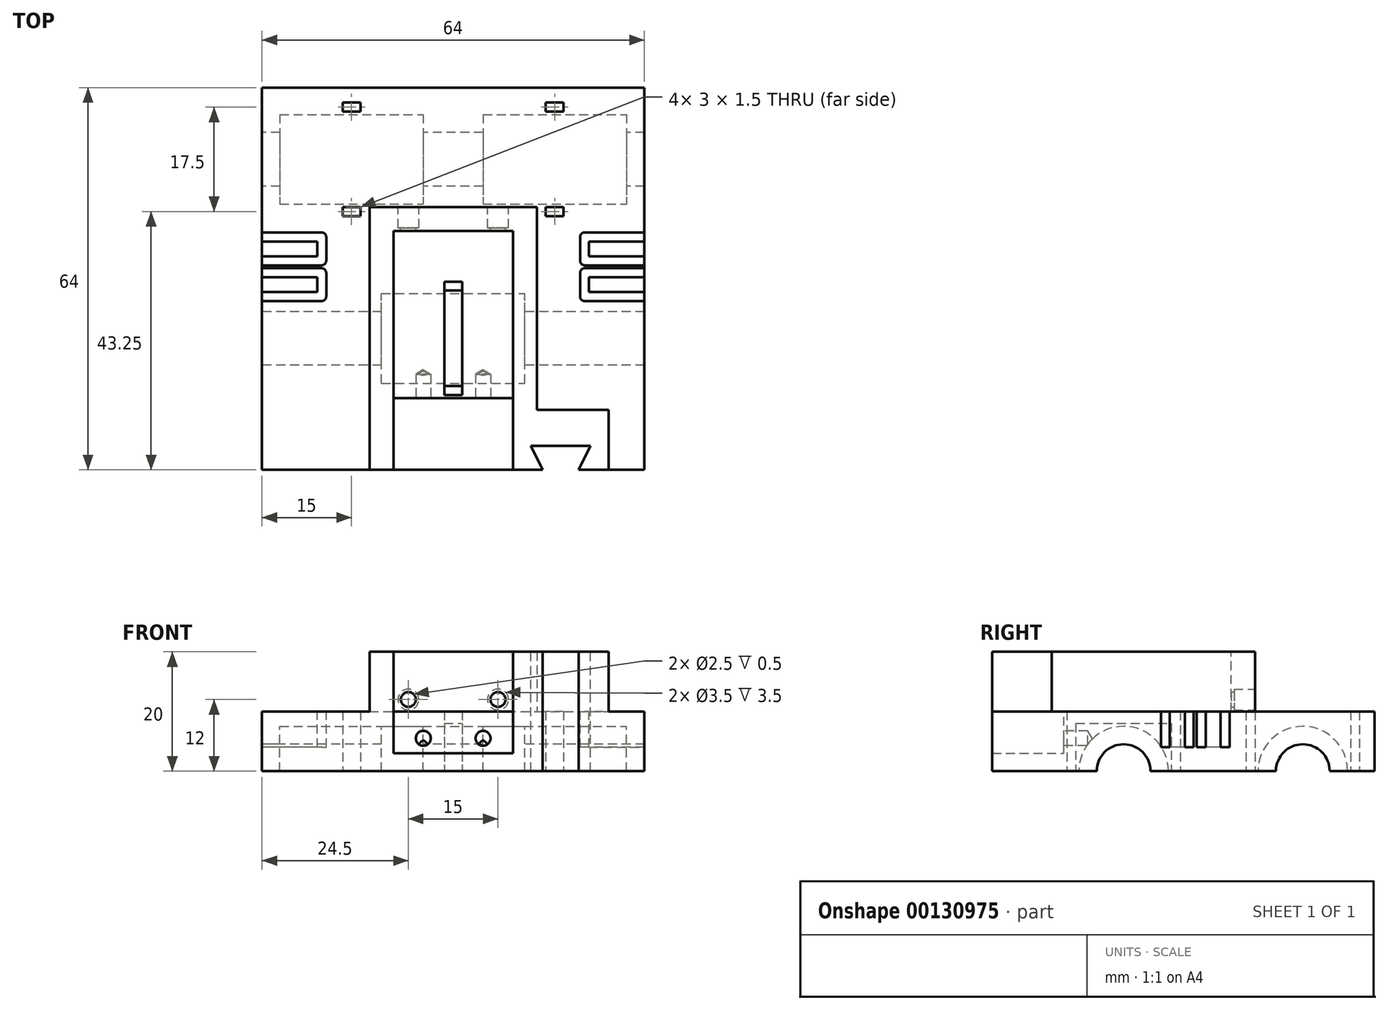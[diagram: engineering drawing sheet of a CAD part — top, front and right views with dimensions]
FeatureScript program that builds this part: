
annotation { "Feature Type Name" : "Feature", "Feature Type Description" : "" }
export const myFeature = defineFeature(function(context is Context, id is Id, definition is map)
    precondition{}
    {
        {
            var Q0;
            Q0=qCreatedBy(makeId("Top.planeOp"),FACE);
            var sketch = newSketch(context, id + "F0", { "sketchPlane" : qUnion([Q0])});
            skLineSegment(sketch, "E0.bottom", {"start": v(0, 0) * mm, "end": v(64, 0) * mm});
            skLineSegment(sketch, "E0.top", {"start": v(0, 64) * mm, "end": v(64, 64) * mm});
            skLineSegment(sketch, "E0.left", {"start": v(0, 0) * mm, "end": v(0, 64) * mm});
            skLineSegment(sketch, "E0.right", {"start": v(64, 0) * mm, "end": v(64, 64) * mm});
            skSolve(sketch);
        }
        {
            var Q0;
            Q0 = qSketchRegion(id + "F0", true);
            extrude(context, id + "F1", {"entities" : qUnion([Q0]), "depth" : 10 * mm});
        }
        {
            var Q0;
            Q0=makeQuery(id+"F1.opExtrude","SWEPT_FACE",FACE,{"disambiguationData":[OSD([sQuery(id+"F0.wireOp",EDGE,"E0.right")])]});
            var sketch = newSketch(context, id + "F2", { "sketchPlane" : qUnion([Q0])});
            skLineSegment(sketch, "E1", {"start": v(37, 15) * mm, "end": v(37, 0) * mm});
            skCircle(sketch, "E2", {"center": v(22, 0) * mm, "radius": 7.5 * mm});
            skCircle(sketch, "E3", {"center": v(52, 0) * mm, "radius": 7.5 * mm});
            skSolve(sketch);
        }
        {
            var Q0;
            {var subQ0=sQuery(id+"F2.wireOp",EDGE,"E2");var subQ1=makeQuery(id+"F1.opExtrude","CAP_EDGE",EDGE,{"disambiguationData":[OSD([sQuery(id+"F0.wireOp",EDGE,"E0.right")])],"isStart":true});var subQ2=makeQuery(id+"F2.imprint","INTERSECT",VERTEX,{"disambiguationData":[OD(0.0)],"derivedFrom":[subQ1,subQ0]});Q0=makeQuery(id+"F2.imprint","IMPRINT",FACE,{"disambiguationData":[TD([[makeQuery(id+"F2.imprint","IMPRINT",EDGE,{"disambiguationData":[TD([[subQ2,1.0]])],"derivedFrom":subQ0}),1.0]])]});}
            var Q1;
            {var subQ0=sQuery(id+"F2.wireOp",EDGE,"E3");var subQ1=makeQuery(id+"F1.opExtrude","CAP_EDGE",EDGE,{"disambiguationData":[OSD([sQuery(id+"F0.wireOp",EDGE,"E0.right")])],"isStart":true});var subQ2=makeQuery(id+"F2.imprint","INTERSECT",VERTEX,{"disambiguationData":[OD(0.0)],"derivedFrom":[subQ1,subQ0]});Q1=makeQuery(id+"F2.imprint","IMPRINT",FACE,{"disambiguationData":[TD([[makeQuery(id+"F2.imprint","IMPRINT",EDGE,{"disambiguationData":[TD([[subQ2,-1.0]])],"derivedFrom":subQ0}),1.0]])]});}
            extrude(context, id + "F3", {"entities" : qUnion([Q0, Q1]), "operationType" : NewBodyOperationType.REMOVE, "endBound" : BoundingType.THROUGH_ALL, "oppositeDirection" : true, "depth" : 25 * mm});
        }
        {
            var Q0;
            {var subQ0=sQuery(id+"F0.wireOp",EDGE,"E0.bottom");var subQ1=sQuery(id+"F0.wireOp",EDGE,"E0.left");var subQ2=sQuery(id+"F0.wireOp",EDGE,"E0.right");Q0=makeQuery(id+"F3.boolean.opBoolean","SPLIT",FACE,{"disambiguationData":[TD([makeQuery(id+"F1.opExtrude","SWEPT_FACE",FACE,{"disambiguationData":[OSD([subQ0])]}),makeQuery(id+"F1.opExtrude","SWEPT_FACE",FACE,{"disambiguationData":[OSD([subQ1])]}),makeQuery(id+"F1.opExtrude","SWEPT_FACE",FACE,{"disambiguationData":[OSD([subQ2])]}),makeQuery(id+"F3.opExtrude","SWEPT_FACE",FACE,{"disambiguationData":[OSD([sQuery(id+"F2.wireOp",EDGE,"E2")])]})])],"derivedFrom":makeQuery(id+"F1.opExtrude","CAP_FACE",FACE,{"disambiguationData":[OSD([subQ0,sQuery(id+"F0.wireOp",EDGE,"E0.top"),subQ1,subQ2])],"isStart":true})});}
            var sketch = newSketch(context, id + "F4", { "sketchPlane" : qUnion([Q0])});
            skLineSegment(sketch, "E4.bottom", {"start": v(0, 0) * mm, "end": v(20, 0) * mm});
            skLineSegment(sketch, "E4.top", {"start": v(0, -34.5) * mm, "end": v(20, -34.5) * mm});
            skLineSegment(sketch, "E4.left", {"start": v(0, 0) * mm, "end": v(0, -34.5) * mm});
            skLineSegment(sketch, "E4.right", {"start": v(20, 0) * mm, "end": v(20, -34.5) * mm});
            skLineSegment(sketch, "E5.bottom", {"start": v(64, 0) * mm, "end": v(44, 0) * mm});
            skLineSegment(sketch, "E5.top", {"start": v(64, -34.5) * mm, "end": v(44, -34.5) * mm});
            skLineSegment(sketch, "E5.left", {"start": v(64, 0) * mm, "end": v(64, -34.5) * mm});
            skLineSegment(sketch, "E5.right", {"start": v(44, 0) * mm, "end": v(44, -34.5) * mm});
            skSolve(sketch);
        }
        {
            var Q0;
            {var subQ0=sQuery(id+"F0.wireOp",EDGE,"E0.top");var subQ1=sQuery(id+"F0.wireOp",EDGE,"E0.left");var subQ2=sQuery(id+"F0.wireOp",EDGE,"E0.right");Q0=makeQuery(id+"F3.boolean.opBoolean","SPLIT",FACE,{"disambiguationData":[TD([makeQuery(id+"F1.opExtrude","SWEPT_FACE",FACE,{"disambiguationData":[OSD([subQ0])]}),makeQuery(id+"F1.opExtrude","SWEPT_FACE",FACE,{"disambiguationData":[OSD([subQ1])]}),makeQuery(id+"F1.opExtrude","SWEPT_FACE",FACE,{"disambiguationData":[OSD([subQ2])]}),makeQuery(id+"F3.opExtrude","SWEPT_FACE",FACE,{"disambiguationData":[OSD([sQuery(id+"F2.wireOp",EDGE,"E3")])]})])],"derivedFrom":makeQuery(id+"F1.opExtrude","CAP_FACE",FACE,{"disambiguationData":[OSD([sQuery(id+"F0.wireOp",EDGE,"E0.bottom"),subQ0,subQ1,subQ2])],"isStart":true})});}
            var sketch = newSketch(context, id + "F5", { "sketchPlane" : qUnion([Q0])});
            skLineSegment(sketch, "E6.bottom", {"start": v(0, -64) * mm, "end": v(3, -64) * mm});
            skLineSegment(sketch, "E6.top", {"start": v(0, -37.3) * mm, "end": v(3, -37.3) * mm});
            skLineSegment(sketch, "E6.left", {"start": v(0, -64) * mm, "end": v(0, -37.3) * mm});
            skLineSegment(sketch, "E6.right", {"start": v(3, -64) * mm, "end": v(3, -37.3) * mm});
            skLineSegment(sketch, "E7.bottom", {"start": v(27, -64) * mm, "end": v(37, -64) * mm});
            skLineSegment(sketch, "E7.top", {"start": v(27, -37.3) * mm, "end": v(37, -37.3) * mm});
            skLineSegment(sketch, "E7.left", {"start": v(27, -64) * mm, "end": v(27, -37.3) * mm});
            skLineSegment(sketch, "E7.right", {"start": v(37, -64) * mm, "end": v(37, -37.3) * mm});
            skLineSegment(sketch, "E8.bottom", {"start": v(64, -64) * mm, "end": v(61, -64) * mm});
            skLineSegment(sketch, "E8.top", {"start": v(64, -37.3) * mm, "end": v(61, -37.3) * mm});
            skLineSegment(sketch, "E8.left", {"start": v(64, -64) * mm, "end": v(64, -37.3) * mm});
            skLineSegment(sketch, "E8.right", {"start": v(61, -64) * mm, "end": v(61, -37.3) * mm});
            skSolve(sketch);
        }
        {
            var Q0;
            Q0 = qSketchRegion(id + "F4", true);
            var Q1;
            Q1 = qSketchRegion(id + "F5", true);
            extrude(context, id + "F6", {"entities" : qUnion([Q0, Q1]), "operationType" : NewBodyOperationType.ADD, "oppositeDirection" : true, "depth" : 7.6 * mm});
        }
        {
            var Q0;
            Q0=makeQuery(id+"F6.boolean.opBoolean","MERGE",FACE,{"derivedFrom":[makeQuery(id+"F1.opExtrude","SWEPT_FACE",FACE,{"disambiguationData":[OSD([sQuery(id+"F0.wireOp",EDGE,"E0.left")])]}),makeQuery(id+"F6.opExtrude","SWEPT_FACE",FACE,{"disambiguationData":[OSD([sQuery(id+"F4.wireOp",EDGE,"E4.left")])]}),makeQuery(id+"F6.opExtrude","SWEPT_FACE",FACE,{"disambiguationData":[OSD([sQuery(id+"F5.wireOp",EDGE,"E6.left")])]})]});
            var sketch = newSketch(context, id + "F7", { "sketchPlane" : qUnion([Q0])});
            skLineSegment(sketch, "E9", {"start": v(-37, 15) * mm, "end": v(-37, 0) * mm});
            skCircle(sketch, "E10", {"center": v(-52, 0) * mm, "radius": 4.5 * mm});
            skCircle(sketch, "E11", {"center": v(-22, 0) * mm, "radius": 4.5 * mm});
            skSolve(sketch);
        }
        {
            var Q0;
            Q0 = qSketchRegion(id + "F7", true);
            extrude(context, id + "F8", {"entities" : qUnion([Q0]), "operationType" : NewBodyOperationType.REMOVE, "endBound" : BoundingType.THROUGH_ALL, "oppositeDirection" : true, "depth" : 25 * mm});
        }
        {
            var Q0;
            Q0=makeQuery(id+"F1.opExtrude","CAP_FACE",FACE,{"disambiguationData":[OSD([sQuery(id+"F0.wireOp",EDGE,"E0.bottom"),sQuery(id+"F0.wireOp",EDGE,"E0.top"),sQuery(id+"F0.wireOp",EDGE,"E0.left"),sQuery(id+"F0.wireOp",EDGE,"E0.right")])],"isStart":false});
            var sketch = newSketch(context, id + "F9", { "sketchPlane" : qUnion([Q0])});
            skLineSegment(sketch, "E12.bottom", {"start": v(18, 0) * mm, "end": v(58, 0) * mm});
            skLineSegment(sketch, "E12.top", {"start": v(18, 44) * mm, "end": v(58, 44) * mm});
            skLineSegment(sketch, "E12.left", {"start": v(18, 0) * mm, "end": v(18, 44) * mm});
            skLineSegment(sketch, "E12.right", {"start": v(58, 0) * mm, "end": v(58, 44) * mm});
            skLineSegment(sketch, "E13.bottom", {"start": v(46, 44) * mm, "end": v(58, 44) * mm});
            skLineSegment(sketch, "E13.top", {"start": v(46, 10) * mm, "end": v(58, 10) * mm});
            skLineSegment(sketch, "E13.left", {"start": v(46, 44) * mm, "end": v(46, 10) * mm});
            skLineSegment(sketch, "E13.right", {"start": v(58, 44) * mm, "end": v(58, 10) * mm});
            skSolve(sketch);
        }
        {
            var Q0;
            Q0=makeQuery(id+"F9.imprint","IMPRINT",FACE,{"disambiguationData":[TD([[makeQuery(id+"F9.imprint","IMPRINT",EDGE,{"derivedFrom":sQuery(id+"F9.wireOp",EDGE,"E12.bottom")}),1.0]])]});
            extrude(context, id + "F10", {"entities" : qUnion([Q0]), "operationType" : NewBodyOperationType.ADD, "depth" : 10 * mm});
        }
        {
            var Q0;
            Q0=makeQuery(id+"F10.opExtrude","CAP_FACE",FACE,{"disambiguationData":[OSD([sQuery(id+"F9.wireOp",EDGE,"E12.bottom"),sQuery(id+"F9.wireOp",EDGE,"E12.top"),sQuery(id+"F9.wireOp",EDGE,"E12.left"),sQuery(id+"F9.wireOp",EDGE,"E12.right")])],"isStart":false});
            var sketch = newSketch(context, id + "F11", { "sketchPlane" : qUnion([Q0])});
            skLineSegment(sketch, "E14.bottom", {"start": v(22, 0) * mm, "end": v(42, 0) * mm});
            skLineSegment(sketch, "E14.top", {"start": v(22, 40) * mm, "end": v(42, 40) * mm});
            skLineSegment(sketch, "E14.left", {"start": v(22, 0) * mm, "end": v(22, 40) * mm});
            skLineSegment(sketch, "E14.right", {"start": v(42, 0) * mm, "end": v(42, 40) * mm});
            skSolve(sketch);
        }
        {
            var Q0;
            Q0 = qSketchRegion(id + "F11", true);
            extrude(context, id + "F12", {"entities" : qUnion([Q0]), "operationType" : NewBodyOperationType.REMOVE, "oppositeDirection" : true, "depth" : 10 * mm});
        }
        {
            var Q0;
            Q0=makeQuery(id+"F12.boolean.opBoolean","COPY",FACE,{"derivedFrom":makeQuery(id+"F12.opExtrude","CAP_FACE",FACE,{"disambiguationData":[OSD([sQuery(id+"F11.wireOp",EDGE,"E14.bottom"),sQuery(id+"F11.wireOp",EDGE,"E14.top"),sQuery(id+"F11.wireOp",EDGE,"E14.left"),sQuery(id+"F11.wireOp",EDGE,"E14.right")])],"isStart":false})});
            var sketch = newSketch(context, id + "F13", { "sketchPlane" : qUnion([Q0])});
            skLineSegment(sketch, "E15.bottom", {"start": v(42, 12) * mm, "end": v(22, 12) * mm});
            skLineSegment(sketch, "E15.top", {"start": v(42, 0) * mm, "end": v(22, 0) * mm});
            skLineSegment(sketch, "E15.left", {"start": v(42, 12) * mm, "end": v(42, 0) * mm});
            skLineSegment(sketch, "E15.right", {"start": v(22, 12) * mm, "end": v(22, 0) * mm});
            skSolve(sketch);
        }
        {
            var Q0;
            Q0 = qSketchRegion(id + "F13", true);
            extrude(context, id + "F14", {"entities" : qUnion([Q0]), "operationType" : NewBodyOperationType.REMOVE, "oppositeDirection" : true, "depth" : 7 * mm});
        }
        {
            var Q0;
            Q0=makeQuery(id+"F10.opExtrude","CAP_FACE",FACE,{"disambiguationData":[OSD([sQuery(id+"F9.wireOp",EDGE,"E12.bottom"),sQuery(id+"F9.wireOp",EDGE,"E12.top"),sQuery(id+"F9.wireOp",EDGE,"E12.left"),sQuery(id+"F9.wireOp",EDGE,"E12.right"),sQuery(id+"F9.wireOp",EDGE,"E13.top"),sQuery(id+"F9.wireOp",EDGE,"E13.left")])],"isStart":false});
            var sketch = newSketch(context, id + "F15", { "sketchPlane" : qUnion([Q0])});
            skLineSegment(sketch, "E16", {"start": v(50, 0) * mm, "end": v(50, 10) * mm});
            skLineSegment(sketch, "E17", {"start": v(47, 0) * mm, "end": v(45, 4) * mm});
            skLineSegment(sketch, "E18", {"start": v(45, 4) * mm, "end": v(55, 4) * mm});
            skLineSegment(sketch, "E19", {"start": v(55, 4) * mm, "end": v(53, 0) * mm});
            skSolve(sketch);
        }
        {
            var Q0;
            {var subQ7=sQuery(id+"F15.wireOp",EDGE,"E17");Q0=makeQuery(id+"F15.imprint","IMPRINT",FACE,{"disambiguationData":[TD([[makeQuery(id+"F15.imprint","IMPRINT",EDGE,{"derivedFrom":subQ7}),-1.0]])]});}
            var Q1;
            {var subQ7=sQuery(id+"F15.wireOp",EDGE,"E19");Q1=makeQuery(id+"F15.imprint","IMPRINT",FACE,{"disambiguationData":[TD([[makeQuery(id+"F15.imprint","IMPRINT",EDGE,{"derivedFrom":subQ7}),-1.0]])]});}
            extrude(context, id + "F16", {"entities" : qUnion([Q0, Q1]), "operationType" : NewBodyOperationType.REMOVE, "endBound" : BoundingType.THROUGH_ALL, "oppositeDirection" : true, "depth" : 25 * mm});
        }
        {
            var Q0;
            Q0=makeQuery(id+"F14.boolean.opBoolean","COPY",FACE,{"derivedFrom":makeQuery(id+"F14.opExtrude","SWEPT_FACE",FACE,{"disambiguationData":[OSD([sQuery(id+"F13.wireOp",EDGE,"E15.bottom")])]})});
            var sketch = newSketch(context, id + "F17", { "sketchPlane" : qUnion([Q0])});
            skLineSegment(sketch, "E20", {"start": v(22, 5.5) * mm, "end": v(42, 5.5) * mm});
            skLineSegment(sketch, "E21", {"start": v(32, 10) * mm, "end": v(32, 3) * mm});
            skPoint(sketch, "E22", {"position": v(27, 5.5) * mm});
            skPoint(sketch, "E23", {"position": v(37, 5.5) * mm});
            skSolve(sketch);
        }
        {
            var Q0;
            Q0=sQuery(id+"F17.wireOp",VERTEX,"E22");
            var Q1;
            Q1=sQuery(id+"F17.wireOp",VERTEX,"E23");
            var Q2;
            Q2=makeQuery(id+"F1.opExtrude","SWEPT_BODY",BODY,{"disambiguationData":[OSD([sQuery(id+"F0.wireOp",EDGE,"E0.bottom"),sQuery(id+"F0.wireOp",EDGE,"E0.top"),sQuery(id+"F0.wireOp",EDGE,"E0.left"),sQuery(id+"F0.wireOp",EDGE,"E0.right")])]});
            hole(context, id + "F18", {"style" : HoleStyle.SIMPLE, "endStyle" : HoleEndStyle.BLIND, "holeDiameter" : 2.5 * mm, "holeDepth" : 4 * mm, "locations" : qUnion([Q0, Q1]), "scope" : qUnion([Q2])});
        }
        {
            var Q0;
            Q0=makeQuery(id+"F10.opExtrude","SWEPT_FACE",FACE,{"disambiguationData":[OSD([sQuery(id+"F9.wireOp",EDGE,"E12.top")])]});
            var sketch = newSketch(context, id + "F19", { "sketchPlane" : qUnion([Q0])});
            skLineSegment(sketch, "E24", {"start": v(-46, 12) * mm, "end": v(-18, 12) * mm});
            skLineSegment(sketch, "E25", {"start": v(-32, 20) * mm, "end": v(-32, 10) * mm});
            skPoint(sketch, "E26", {"position": v(-39.5, 12) * mm});
            skPoint(sketch, "E27", {"position": v(-24.5, 12) * mm});
            skSolve(sketch);
        }
        {
            var Q0;
            Q0=sQuery(id+"F19.wireOp",VERTEX,"E26");
            var Q1;
            Q1=sQuery(id+"F19.wireOp",VERTEX,"E27");
            var Q2;
            Q2=makeQuery(id+"F1.opExtrude","SWEPT_BODY",BODY,{"disambiguationData":[OSD([sQuery(id+"F0.wireOp",EDGE,"E0.bottom"),sQuery(id+"F0.wireOp",EDGE,"E0.top"),sQuery(id+"F0.wireOp",EDGE,"E0.left"),sQuery(id+"F0.wireOp",EDGE,"E0.right")])]});
            hole(context, id + "F20", {"style" : HoleStyle.C_BORE, "endStyle" : HoleEndStyle.BLIND, "holeDiameter" : 2.5 * mm, "cBoreDiameter" : 3.5 * mm, "cBoreDepth" : 3.5 * mm, "holeDepth" : 4 * mm, "locations" : qUnion([Q0, Q1]), "scope" : qUnion([Q2])});
        }
        {
            var Q0;
            Q0=makeQuery(id+"F1.opExtrude","CAP_FACE",FACE,{"disambiguationData":[OSD([sQuery(id+"F0.wireOp",EDGE,"E0.bottom"),sQuery(id+"F0.wireOp",EDGE,"E0.top"),sQuery(id+"F0.wireOp",EDGE,"E0.left"),sQuery(id+"F0.wireOp",EDGE,"E0.right")])],"isStart":false});
            var sketch = newSketch(context, id + "F21", { "sketchPlane" : qUnion([Q0])});
            skLineSegment(sketch, "E28", {"start": v(32, 64) * mm, "end": v(32, 0) * mm});
            skLineSegment(sketch, "E29", {"start": v(0, 32) * mm, "end": v(64, 32) * mm});
            skLineSegment(sketch, "E30", {"start": v(0, 39) * mm, "end": v(10, 39) * mm});
            skLineSegment(sketch, "E31", {"start": v(10, 39) * mm, "end": v(10, 35) * mm});
            skLineSegment(sketch, "E32", {"start": v(10, 35) * mm, "end": v(0, 35) * mm});
            skLineSegment(sketch, "E33", {"start": v(0, 33) * mm, "end": v(10, 33) * mm});
            skLineSegment(sketch, "E34", {"start": v(10, 33) * mm, "end": v(10, 29) * mm});
            skLineSegment(sketch, "E35", {"start": v(10, 29) * mm, "end": v(0, 29) * mm});
            skLineSegment(sketch, "E36.MirrorCS", {"start": v(54, 29) * mm, "end": v(64, 29) * mm});
            skLineSegment(sketch, "E37.MirrorCS", {"start": v(54, 33) * mm, "end": v(54, 29) * mm});
            skLineSegment(sketch, "E38.MirrorCS", {"start": v(64, 33) * mm, "end": v(54, 33) * mm});
            skLineSegment(sketch, "E39.MirrorCS", {"start": v(54, 35) * mm, "end": v(64, 35) * mm});
            skLineSegment(sketch, "E40.MirrorCS", {"start": v(64, 39) * mm, "end": v(54, 39) * mm});
            skLineSegment(sketch, "E41.MirrorCS", {"start": v(54, 39) * mm, "end": v(54, 35) * mm});
            skArc(sketch, "E42.0.startCap", {"start": v(10, 35.75) * mm, "mid": v(10.75, 35) * mm, "end": v(10, 34.25) * mm});
            skArc(sketch, "E42.0.endCap", {"start": v(0, 34.25) * mm, "mid": v(-0.75, 35) * mm, "end": v(0, 35.75) * mm});
            skLineSegment(sketch, "E42.0.left", {"start": v(10, 34.25) * mm, "end": v(0, 34.25) * mm});
            skLineSegment(sketch, "E42.0.right", {"start": v(10, 35.75) * mm, "end": v(0, 35.75) * mm});
            skArc(sketch, "E42.1.startCap", {"start": v(0, 38.25) * mm, "mid": v(-0.75, 39) * mm, "end": v(0, 39.75) * mm});
            skArc(sketch, "E42.1.endCap", {"start": v(10, 39.75) * mm, "mid": v(10.75, 39) * mm, "end": v(10, 38.25) * mm});
            skLineSegment(sketch, "E42.1.left", {"start": v(0, 39.75) * mm, "end": v(10, 39.75) * mm});
            skLineSegment(sketch, "E42.1.right", {"start": v(0, 38.25) * mm, "end": v(10, 38.25) * mm});
            skArc(sketch, "E42.2.startCap", {"start": v(9.25, 39) * mm, "mid": v(10, 39.75) * mm, "end": v(10.75, 39) * mm});
            skArc(sketch, "E42.2.endCap", {"start": v(10.75, 35) * mm, "mid": v(10, 34.25) * mm, "end": v(9.25, 35) * mm});
            skLineSegment(sketch, "E42.2.left", {"start": v(10.75, 39) * mm, "end": v(10.75, 35) * mm});
            skLineSegment(sketch, "E42.2.right", {"start": v(9.25, 39) * mm, "end": v(9.25, 35) * mm});
            skArc(sketch, "E42.3.startCap", {"start": v(9.25, 33) * mm, "mid": v(10, 33.75) * mm, "end": v(10.75, 33) * mm});
            skArc(sketch, "E42.3.endCap", {"start": v(10.75, 29) * mm, "mid": v(10, 28.25) * mm, "end": v(9.25, 29) * mm});
            skLineSegment(sketch, "E42.3.left", {"start": v(10.75, 33) * mm, "end": v(10.75, 29) * mm});
            skLineSegment(sketch, "E42.3.right", {"start": v(9.25, 33) * mm, "end": v(9.25, 29) * mm});
            skArc(sketch, "E42.4.startCap", {"start": v(0, 32.25) * mm, "mid": v(-0.75, 33) * mm, "end": v(0, 33.75) * mm});
            skArc(sketch, "E42.4.endCap", {"start": v(10, 33.75) * mm, "mid": v(10.75, 33) * mm, "end": v(10, 32.25) * mm});
            skLineSegment(sketch, "E42.4.left", {"start": v(0, 33.75) * mm, "end": v(10, 33.75) * mm});
            skLineSegment(sketch, "E42.4.right", {"start": v(0, 32.25) * mm, "end": v(10, 32.25) * mm});
            skArc(sketch, "E42.5.startCap", {"start": v(10, 29.75) * mm, "mid": v(10.75, 29) * mm, "end": v(10, 28.25) * mm});
            skArc(sketch, "E42.5.endCap", {"start": v(0, 28.25) * mm, "mid": v(-0.75, 29) * mm, "end": v(0, 29.75) * mm});
            skLineSegment(sketch, "E42.5.left", {"start": v(10, 28.25) * mm, "end": v(0, 28.25) * mm});
            skLineSegment(sketch, "E42.5.right", {"start": v(10, 29.75) * mm, "end": v(0, 29.75) * mm});
            skArc(sketch, "E43.0.startCap", {"start": v(64, 39.75) * mm, "mid": v(64.75, 39) * mm, "end": v(64, 38.25) * mm});
            skArc(sketch, "E43.0.endCap", {"start": v(54, 38.25) * mm, "mid": v(53.25, 39) * mm, "end": v(54, 39.75) * mm});
            skLineSegment(sketch, "E43.0.left", {"start": v(64, 38.25) * mm, "end": v(54, 38.25) * mm});
            skLineSegment(sketch, "E43.0.right", {"start": v(64, 39.75) * mm, "end": v(54, 39.75) * mm});
            skArc(sketch, "E43.1.startCap", {"start": v(53.25, 39) * mm, "mid": v(54, 39.75) * mm, "end": v(54.75, 39) * mm});
            skArc(sketch, "E43.1.endCap", {"start": v(54.75, 35) * mm, "mid": v(54, 34.25) * mm, "end": v(53.25, 35) * mm});
            skLineSegment(sketch, "E43.1.left", {"start": v(54.75, 39) * mm, "end": v(54.75, 35) * mm});
            skLineSegment(sketch, "E43.1.right", {"start": v(53.25, 39) * mm, "end": v(53.25, 35) * mm});
            skArc(sketch, "E43.2.startCap", {"start": v(54, 34.25) * mm, "mid": v(53.25, 35) * mm, "end": v(54, 35.75) * mm});
            skArc(sketch, "E43.2.endCap", {"start": v(64, 35.75) * mm, "mid": v(64.75, 35) * mm, "end": v(64, 34.25) * mm});
            skLineSegment(sketch, "E43.2.left", {"start": v(54, 35.75) * mm, "end": v(64, 35.75) * mm});
            skLineSegment(sketch, "E43.2.right", {"start": v(54, 34.25) * mm, "end": v(64, 34.25) * mm});
            skArc(sketch, "E43.3.startCap", {"start": v(64, 33.75) * mm, "mid": v(64.75, 33) * mm, "end": v(64, 32.25) * mm});
            skArc(sketch, "E43.3.endCap", {"start": v(54, 32.25) * mm, "mid": v(53.25, 33) * mm, "end": v(54, 33.75) * mm});
            skLineSegment(sketch, "E43.3.left", {"start": v(64, 32.25) * mm, "end": v(54, 32.25) * mm});
            skLineSegment(sketch, "E43.3.right", {"start": v(64, 33.75) * mm, "end": v(54, 33.75) * mm});
            skArc(sketch, "E43.4.startCap", {"start": v(53.25, 33) * mm, "mid": v(54, 33.75) * mm, "end": v(54.75, 33) * mm});
            skArc(sketch, "E43.4.endCap", {"start": v(54.75, 29) * mm, "mid": v(54, 28.25) * mm, "end": v(53.25, 29) * mm});
            skLineSegment(sketch, "E43.4.left", {"start": v(54.75, 33) * mm, "end": v(54.75, 29) * mm});
            skLineSegment(sketch, "E43.4.right", {"start": v(53.25, 33) * mm, "end": v(53.25, 29) * mm});
            skArc(sketch, "E43.5.startCap", {"start": v(54, 28.25) * mm, "mid": v(53.25, 29) * mm, "end": v(54, 29.75) * mm});
            skArc(sketch, "E43.5.endCap", {"start": v(64, 29.75) * mm, "mid": v(64.75, 29) * mm, "end": v(64, 28.25) * mm});
            skLineSegment(sketch, "E43.5.left", {"start": v(54, 29.75) * mm, "end": v(64, 29.75) * mm});
            skLineSegment(sketch, "E43.5.right", {"start": v(54, 28.25) * mm, "end": v(64, 28.25) * mm});
            skSolve(sketch);
        }
        {
            var Q0;
            Q0 = qSketchRegion(id + "F21", true);
            extrude(context, id + "F22", {"entities" : qUnion([Q0]), "operationType" : NewBodyOperationType.REMOVE, "oppositeDirection" : true, "depth" : 6 * mm});
        }
        {
            var Q0;
            {var subQ0=sQuery(id+"F5.wireOp",EDGE,"E6.right");var subQ1=sQuery(id+"F5.wireOp",EDGE,"E6.left");var subQ2=sQuery(id+"F4.wireOp",EDGE,"E5.right");var subQ3=sQuery(id+"F0.wireOp",EDGE,"E0.left");var subQ4=makeQuery(id+"F1.opExtrude","SWEPT_FACE",FACE,{"disambiguationData":[OSD([subQ3])]});var subQ5=sQuery(id+"F4.wireOp",EDGE,"E4.right");var subQ6=sQuery(id+"F4.wireOp",EDGE,"E5.left");var subQ7=sQuery(id+"F0.wireOp",EDGE,"E0.right");var subQ8=makeQuery(id+"F1.opExtrude","SWEPT_FACE",FACE,{"disambiguationData":[OSD([subQ7])]});var subQ9=sQuery(id+"F5.wireOp",EDGE,"E7.right");var subQ10=sQuery(id+"F4.wireOp",EDGE,"E4.left");var subQ11=makeQuery(id+"F3.opExtrude","SWEPT_FACE",FACE,{"disambiguationData":[OSD([sQuery(id+"F2.wireOp",EDGE,"E2")])]});var subQ12=makeQuery(id+"F3.opExtrude","SWEPT_FACE",FACE,{"disambiguationData":[OSD([sQuery(id+"F2.wireOp",EDGE,"E3")])]});var subQ13=sQuery(id+"F5.wireOp",EDGE,"E7.left");var subQ14=sQuery(id+"F5.wireOp",EDGE,"E8.left");var subQ15=sQuery(id+"F5.wireOp",EDGE,"E8.right");var subQ16=sQuery(id+"F0.wireOp",EDGE,"E0.top");var subQ17=sQuery(id+"F0.wireOp",EDGE,"E0.bottom");var subQ18=makeQuery(id+"F1.opExtrude","CAP_FACE",FACE,{"disambiguationData":[OSD([subQ17,subQ16,subQ3,subQ7])],"isStart":true});Q0=makeQuery(id+"F8.boolean.opBoolean","SPLIT",FACE,{"disambiguationData":[TD([subQ4,subQ8,makeQuery(id+"F3.boolean.opBoolean","COPY",FACE,{"derivedFrom":subQ11}),makeQuery(id+"F3.boolean.opBoolean","COPY",FACE,{"derivedFrom":subQ12}),makeQuery(id+"F6.opExtrude","SWEPT_FACE",FACE,{"disambiguationData":[OSD([subQ10])]}),makeQuery(id+"F6.opExtrude","SWEPT_FACE",FACE,{"disambiguationData":[OSD([subQ5])]}),makeQuery(id+"F6.opExtrude","SWEPT_FACE",FACE,{"disambiguationData":[OSD([subQ6])]}),makeQuery(id+"F6.opExtrude","SWEPT_FACE",FACE,{"disambiguationData":[OSD([subQ2])]}),makeQuery(id+"F6.opExtrude","SWEPT_FACE",FACE,{"disambiguationData":[OSD([subQ1])]}),makeQuery(id+"F6.opExtrude","SWEPT_FACE",FACE,{"disambiguationData":[OSD([subQ0])]}),makeQuery(id+"F6.opExtrude","SWEPT_FACE",FACE,{"disambiguationData":[OSD([subQ13])]}),makeQuery(id+"F6.opExtrude","SWEPT_FACE",FACE,{"disambiguationData":[OSD([subQ9])]}),makeQuery(id+"F6.opExtrude","SWEPT_FACE",FACE,{"disambiguationData":[OSD([subQ14])]}),makeQuery(id+"F6.opExtrude","SWEPT_FACE",FACE,{"disambiguationData":[OSD([subQ15])]}),makeQuery(id+"F8.opExtrude","SWEPT_FACE",FACE,{"disambiguationData":[OSD([sQuery(id+"F7.wireOp",EDGE,"E10")])]}),makeQuery(id+"F8.opExtrude","SWEPT_FACE",FACE,{"disambiguationData":[OSD([sQuery(id+"F7.wireOp",EDGE,"E11")])]})])],"derivedFrom":makeQuery(id+"F6.boolean.opBoolean","MERGE",FACE,{"derivedFrom":[makeQuery(id+"F3.boolean.opBoolean","SPLIT",FACE,{"disambiguationData":[TD([makeQuery(id+"F1.opExtrude","SWEPT_FACE",FACE,{"disambiguationData":[OSD([subQ17])]}),subQ4,subQ8,subQ11])],"derivedFrom":subQ18}),makeQuery(id+"F3.boolean.opBoolean","SPLIT",FACE,{"disambiguationData":[TD([makeQuery(id+"F1.opExtrude","SWEPT_FACE",FACE,{"disambiguationData":[OSD([subQ16])]}),subQ4,subQ8,subQ12])],"derivedFrom":subQ18}),makeQuery(id+"F3.boolean.opBoolean","SPLIT",FACE,{"disambiguationData":[TD([subQ4,subQ8,subQ11,subQ12])],"derivedFrom":subQ18}),makeQuery(id+"F6.opExtrude","CAP_FACE",FACE,{"disambiguationData":[OSD([sQuery(id+"F4.wireOp",EDGE,"E4.bottom"),sQuery(id+"F4.wireOp",EDGE,"E4.top"),subQ10,subQ5])],"isStart":true}),makeQuery(id+"F6.opExtrude","CAP_FACE",FACE,{"disambiguationData":[OSD([sQuery(id+"F4.wireOp",EDGE,"E5.bottom"),sQuery(id+"F4.wireOp",EDGE,"E5.top"),subQ6,subQ2])],"isStart":true}),makeQuery(id+"F6.opExtrude","CAP_FACE",FACE,{"disambiguationData":[OSD([sQuery(id+"F5.wireOp",EDGE,"E6.bottom"),sQuery(id+"F5.wireOp",EDGE,"E6.top"),subQ1,subQ0])],"isStart":true}),makeQuery(id+"F6.opExtrude","CAP_FACE",FACE,{"disambiguationData":[OSD([sQuery(id+"F5.wireOp",EDGE,"E7.bottom"),sQuery(id+"F5.wireOp",EDGE,"E7.top"),subQ13,subQ9])],"isStart":true}),makeQuery(id+"F6.opExtrude","CAP_FACE",FACE,{"disambiguationData":[OSD([sQuery(id+"F5.wireOp",EDGE,"E8.bottom"),sQuery(id+"F5.wireOp",EDGE,"E8.top"),subQ14,subQ15])],"isStart":true})]})});}
            var sketch = newSketch(context, id + "F23", { "sketchPlane" : qUnion([Q0])});
            skLineSegment(sketch, "E44.bottom", {"start": v(13.5, -44) * mm, "end": v(16.5, -44) * mm});
            skLineSegment(sketch, "E44.top", {"start": v(13.5, -42.5) * mm, "end": v(16.5, -42.5) * mm});
            skLineSegment(sketch, "E44.left", {"start": v(13.5, -44) * mm, "end": v(13.5, -42.5) * mm});
            skLineSegment(sketch, "E44.right", {"start": v(16.5, -44) * mm, "end": v(16.5, -42.5) * mm});
            skLineSegment(sketch, "E45.bottom", {"start": v(13.5, -60) * mm, "end": v(16.5, -60) * mm});
            skLineSegment(sketch, "E45.top", {"start": v(13.5, -61.5) * mm, "end": v(16.5, -61.5) * mm});
            skLineSegment(sketch, "E45.left", {"start": v(13.5, -60) * mm, "end": v(13.5, -61.5) * mm});
            skLineSegment(sketch, "E45.right", {"start": v(16.5, -60) * mm, "end": v(16.5, -61.5) * mm});
            skLineSegment(sketch, "E46", {"start": v(32, -29.5) * mm, "end": v(32, -47.5) * mm});
            skLineSegment(sketch, "E47", {"start": v(15, -44.5) * mm, "end": v(15, -68.74) * mm});
            skLineSegment(sketch, "E48.MirrorCS", {"start": v(50.5, -42.5) * mm, "end": v(47.5, -42.5) * mm});
            skLineSegment(sketch, "E49.MirrorCS", {"start": v(47.5, -44) * mm, "end": v(47.5, -42.5) * mm});
            skLineSegment(sketch, "E50.MirrorCS", {"start": v(50.5, -44) * mm, "end": v(47.5, -44) * mm});
            skLineSegment(sketch, "E51.MirrorCS", {"start": v(50.5, -44) * mm, "end": v(50.5, -42.5) * mm});
            skLineSegment(sketch, "E52.MirrorCS", {"start": v(50.5, -61.5) * mm, "end": v(47.5, -61.5) * mm});
            skLineSegment(sketch, "E53.MirrorCS", {"start": v(47.5, -60) * mm, "end": v(47.5, -61.5) * mm});
            skLineSegment(sketch, "E54.MirrorCS", {"start": v(50.5, -60) * mm, "end": v(47.5, -60) * mm});
            skLineSegment(sketch, "E55.MirrorCS", {"start": v(50.5, -60) * mm, "end": v(50.5, -61.5) * mm});
            skLineSegment(sketch, "E56.bottom", {"start": v(30.5, -30) * mm, "end": v(33.5, -30) * mm});
            skLineSegment(sketch, "E56.top", {"start": v(30.5, -31.5) * mm, "end": v(33.5, -31.5) * mm});
            skLineSegment(sketch, "E56.left", {"start": v(30.5, -30) * mm, "end": v(30.5, -31.5) * mm});
            skLineSegment(sketch, "E56.right", {"start": v(33.5, -30) * mm, "end": v(33.5, -31.5) * mm});
            skLineSegment(sketch, "E57", {"start": v(14.96, -22) * mm, "end": v(49.37, -22) * mm});
            skLineSegment(sketch, "E58.MirrorCS", {"start": v(33.5, -14) * mm, "end": v(33.5, -12.5) * mm});
            skLineSegment(sketch, "E59.MirrorCS", {"start": v(30.5, -14) * mm, "end": v(33.5, -14) * mm});
            skLineSegment(sketch, "E60.MirrorCS", {"start": v(30.5, -12.5) * mm, "end": v(33.5, -12.5) * mm});
            skLineSegment(sketch, "E61.MirrorCS", {"start": v(30.5, -14) * mm, "end": v(30.5, -12.5) * mm});
            skSolve(sketch);
        }
        {
            var Q0;
            Q0=makeQuery(id+"F23.imprint","IMPRINT",FACE,{"disambiguationData":[TD([[makeQuery(id+"F23.imprint","IMPRINT",EDGE,{"derivedFrom":sQuery(id+"F23.wireOp",EDGE,"E48.MirrorCS")}),1.0]])]});
            var Q1;
            Q1=makeQuery(id+"F23.imprint","IMPRINT",FACE,{"disambiguationData":[TD([[makeQuery(id+"F23.imprint","IMPRINT",EDGE,{"derivedFrom":sQuery(id+"F23.wireOp",EDGE,"E52.MirrorCS")}),-1.0]])]});
            var Q2;
            {var subQ0=sQuery(id+"F23.wireOp",EDGE,"E45.left");Q2=makeQuery(id+"F23.imprint","IMPRINT",FACE,{"disambiguationData":[TD([[makeQuery(id+"F23.imprint","IMPRINT",EDGE,{"derivedFrom":subQ0}),1.0]])]});}
            var Q3;
            {var subQ0=sQuery(id+"F23.wireOp",EDGE,"E45.right");Q3=makeQuery(id+"F23.imprint","IMPRINT",FACE,{"disambiguationData":[TD([[makeQuery(id+"F23.imprint","IMPRINT",EDGE,{"derivedFrom":subQ0}),-1.0]])]});}
            var Q4;
            Q4=makeQuery(id+"F23.imprint","IMPRINT",FACE,{"disambiguationData":[TD([[makeQuery(id+"F23.imprint","IMPRINT",EDGE,{"derivedFrom":sQuery(id+"F23.wireOp",EDGE,"E44.bottom")}),1.0]])]});
            var Q5;
            {var subQ5=sQuery(id+"F23.wireOp",EDGE,"E56.right");Q5=makeQuery(id+"F23.imprint","IMPRINT",FACE,{"disambiguationData":[TD([[makeQuery(id+"F23.imprint","IMPRINT",EDGE,{"derivedFrom":subQ5}),-1.0]])]});}
            var Q6;
            {var subQ5=sQuery(id+"F23.wireOp",EDGE,"E56.left");Q6=makeQuery(id+"F23.imprint","IMPRINT",FACE,{"disambiguationData":[TD([[makeQuery(id+"F23.imprint","IMPRINT",EDGE,{"derivedFrom":subQ5}),1.0]])]});}
            var Q7;
            Q7=makeQuery(id+"F23.imprint","IMPRINT",FACE,{"disambiguationData":[TD([[makeQuery(id+"F23.imprint","IMPRINT",EDGE,{"derivedFrom":sQuery(id+"F23.wireOp",EDGE,"E58.MirrorCS")}),1.0]])]});
            var Q8;
            {var subQ0=sQuery(id+"F0.wireOp",EDGE,"E0.right");var subQ1=sQuery(id+"F0.wireOp",EDGE,"E0.bottom");var subQ2=sQuery(id+"F0.wireOp",EDGE,"E0.left");var subQ3=sQuery(id+"F0.wireOp",EDGE,"E0.top");Q8=makeQuery(id+"F22.boolean.opBoolean","SPLIT",FACE,{"disambiguationData":[TD([makeQuery(id+"F1.opExtrude","SWEPT_FACE",FACE,{"disambiguationData":[OSD([subQ1])]})])],"derivedFrom":makeQuery(id+"F1.opExtrude","CAP_FACE",FACE,{"disambiguationData":[OSD([subQ1,subQ3,subQ2,subQ0])],"isStart":false})});}
            extrude(context, id + "F24", {"entities" : qUnion([Q0, Q1, Q2, Q3, Q4, Q5, Q6, Q7]), "operationType" : NewBodyOperationType.REMOVE, "endBound" : BoundingType.UP_TO_SURFACE, "oppositeDirection" : true, "endBoundEntityFace" : qUnion([Q8]), "depth" : 25 * mm});
        }
        {
            var Q0;
            Q0=makeQuery(id+"F12.boolean.opBoolean","COPY",FACE,{"derivedFrom":makeQuery(id+"F12.opExtrude","CAP_FACE",FACE,{"disambiguationData":[OSD([sQuery(id+"F11.wireOp",EDGE,"E14.bottom"),sQuery(id+"F11.wireOp",EDGE,"E14.top"),sQuery(id+"F11.wireOp",EDGE,"E14.left"),sQuery(id+"F11.wireOp",EDGE,"E14.right")])],"isStart":false})});
            var sketch = newSketch(context, id + "F25", { "sketchPlane" : qUnion([Q0])});
            skLineSegment(sketch, "E62.bottom", {"start": v(33.5, 14) * mm, "end": v(30.5, 14) * mm});
            skLineSegment(sketch, "E62.top", {"start": v(33.5, 30) * mm, "end": v(30.5, 30) * mm});
            skLineSegment(sketch, "E62.left", {"start": v(33.5, 14) * mm, "end": v(33.5, 30) * mm});
            skLineSegment(sketch, "E62.right", {"start": v(30.5, 14) * mm, "end": v(30.5, 30) * mm});
            skSolve(sketch);
        }
        {
            var Q0;
            Q0 = qSketchRegion(id + "F25", true);
            extrude(context, id + "F26", {"entities" : qUnion([Q0]), "operationType" : NewBodyOperationType.REMOVE, "oppositeDirection" : true, "depth" : 2 * mm});
        }
    });
